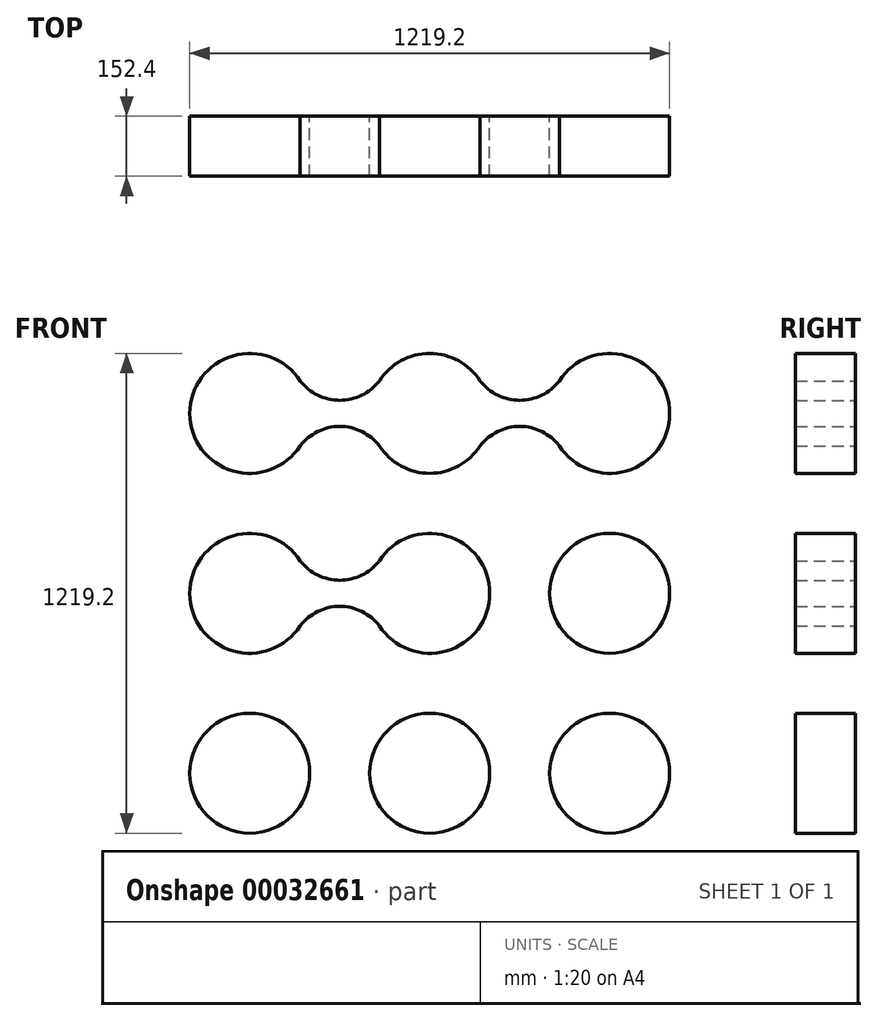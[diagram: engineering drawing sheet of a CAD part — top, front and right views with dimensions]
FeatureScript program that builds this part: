
annotation { "Feature Type Name" : "Feature", "Feature Type Description" : "" }
export const myFeature = defineFeature(function(context is Context, id is Id, definition is map)
    precondition{}
    {
        {
            var Q0;
            Q0=qCreatedBy(makeId("Front.planeOp"),FACE);
            var sketch = newSketch(context, id + "F0", { "sketchPlane" : qUnion([Q0])});
            skArc(sketch, "E0", {"start": v(-128.1, -82.55) * mm, "mid": v(152.4, 0) * mm, "end": v(-128.1, 82.55) * mm});
            skLineSegment(sketch, "E1", {"start": v(0, 0) * mm, "end": v(457.2, 0) * mm, "construction": true});
            skLineSegment(sketch, "E2", {"start": v(0, 0) * mm, "end": v(-457.2, 0) * mm, "construction": true});
            skCircle(sketch, "E3", {"center": v(457.2, 0) * mm, "radius": 152.4 * mm});
            skArc(sketch, "E4", {"start": v(-329.1, 82.55) * mm, "mid": v(-609.6, 0) * mm, "end": v(-329.1, -82.55) * mm});
            skLineSegment(sketch, "E5", {"start": v(457.2, 0) * mm, "end": v(457.2, -457.2) * mm, "construction": true});
            skCircle(sketch, "E6", {"center": v(457.2, -457.2) * mm, "radius": 152.4 * mm});
            skLineSegment(sketch, "E7", {"start": v(457.2, -457.2) * mm, "end": v(0, -457.2) * mm, "construction": true});
            skLineSegment(sketch, "E8", {"start": v(0, -457.2) * mm, "end": v(-457.2, -457.2) * mm, "construction": true});
            skCircle(sketch, "E9", {"center": v(0, -457.2) * mm, "radius": 152.4 * mm});
            skCircle(sketch, "E10", {"center": v(-457.2, -457.2) * mm, "radius": 152.4 * mm});
            skLineSegment(sketch, "E11", {"start": v(457.2, 0) * mm, "end": v(457.2, 457.2) * mm, "construction": true});
            skLineSegment(sketch, "E12", {"start": v(457.2, 457.2) * mm, "end": v(0, 457.2) * mm, "construction": true});
            skLineSegment(sketch, "E13", {"start": v(0, 457.2) * mm, "end": v(-457.2, 457.2) * mm, "construction": true});
            skArc(sketch, "E14", {"start": v(-329.1, 539.75) * mm, "mid": v(-609.6, 457.2) * mm, "end": v(-329.1, 374.65) * mm});
            skArc(sketch, "E15", {"start": v(-128.1, 374.65) * mm, "mid": v(0, 304.8) * mm, "end": v(128.1, 374.65) * mm});
            skArc(sketch, "E16", {"start": v(329.1, 374.65) * mm, "mid": v(609.6, 457.2) * mm, "end": v(329.1, 539.75) * mm});
            skLineSegment(sketch, "E17.0", {"start": v(-128.1, 82.55) * mm, "end": v(-329.1, 82.55) * mm, "construction": true});
            skArc(sketch, "E18", {"start": v(-329.1, 82.55) * mm, "mid": v(-228.6, 33.2) * mm, "end": v(-128.1, 82.55) * mm});
            skArc(sketch, "E19.MirrorCS", {"start": v(-329.1, -82.55) * mm, "mid": v(-228.6, -33.2) * mm, "end": v(-128.1, -82.55) * mm});
            skLineSegment(sketch, "E20.0", {"start": v(-128.1, 539.75) * mm, "end": v(-329.1, 539.75) * mm, "construction": true});
            skLineSegment(sketch, "E21.0", {"start": v(329.1, 539.75) * mm, "end": v(128.1, 539.75) * mm, "construction": true});
            skArc(sketch, "E22", {"start": v(-329.1, 539.75) * mm, "mid": v(-228.6, 490.4) * mm, "end": v(-128.1, 539.75) * mm});
            skArc(sketch, "E23", {"start": v(128.1, 539.75) * mm, "mid": v(228.6, 490.4) * mm, "end": v(329.1, 539.75) * mm});
            skArc(sketch, "E24.MirrorCS", {"start": v(128.1, 374.65) * mm, "mid": v(228.6, 424) * mm, "end": v(329.1, 374.65) * mm});
            skArc(sketch, "E25.MirrorCS", {"start": v(-329.1, 374.65) * mm, "mid": v(-228.6, 424) * mm, "end": v(-128.1, 374.65) * mm});
            skArc(sketch, "E26.trimOffspring", {"start": v(128.1, 539.75) * mm, "mid": v(0, 609.6) * mm, "end": v(-128.1, 539.75) * mm});
            skSolve(sketch);
        }
        {
            var Q0;
            Q0=makeQuery(id+"F0.imprint","IMPRINT",FACE,{"disambiguationData":[TD([[makeQuery(id+"F0.imprint","IMPRINT",EDGE,{"derivedFrom":sQuery(id+"F0.wireOp",EDGE,"E14")}),1.0]])]});
            var Q1;
            Q1=makeQuery(id+"F0.imprint","IMPRINT",FACE,{"disambiguationData":[TD([[makeQuery(id+"F0.imprint","IMPRINT",EDGE,{"derivedFrom":sQuery(id+"F0.wireOp",EDGE,"E0")}),1.0]])]});
            var Q2;
            Q2=makeQuery(id+"F0.imprint","IMPRINT",FACE,{"disambiguationData":[TD([[makeQuery(id+"F0.imprint","IMPRINT",EDGE,{"derivedFrom":sQuery(id+"F0.wireOp",EDGE,"E3")}),1.0]])]});
            var Q3;
            Q3=makeQuery(id+"F0.imprint","IMPRINT",FACE,{"disambiguationData":[TD([[makeQuery(id+"F0.imprint","IMPRINT",EDGE,{"derivedFrom":sQuery(id+"F0.wireOp",EDGE,"E6")}),1.0]])]});
            var Q4;
            Q4=makeQuery(id+"F0.imprint","IMPRINT",FACE,{"disambiguationData":[TD([[makeQuery(id+"F0.imprint","IMPRINT",EDGE,{"derivedFrom":sQuery(id+"F0.wireOp",EDGE,"E9")}),1.0]])]});
            var Q5;
            Q5=makeQuery(id+"F0.imprint","IMPRINT",FACE,{"disambiguationData":[TD([[makeQuery(id+"F0.imprint","IMPRINT",EDGE,{"derivedFrom":sQuery(id+"F0.wireOp",EDGE,"E10")}),1.0]])]});
            extrude(context, id + "F1", {"entities" : qUnion([Q0, Q1, Q2, Q3, Q4, Q5]), "depth" : 152.4 * mm});
        }
    });
